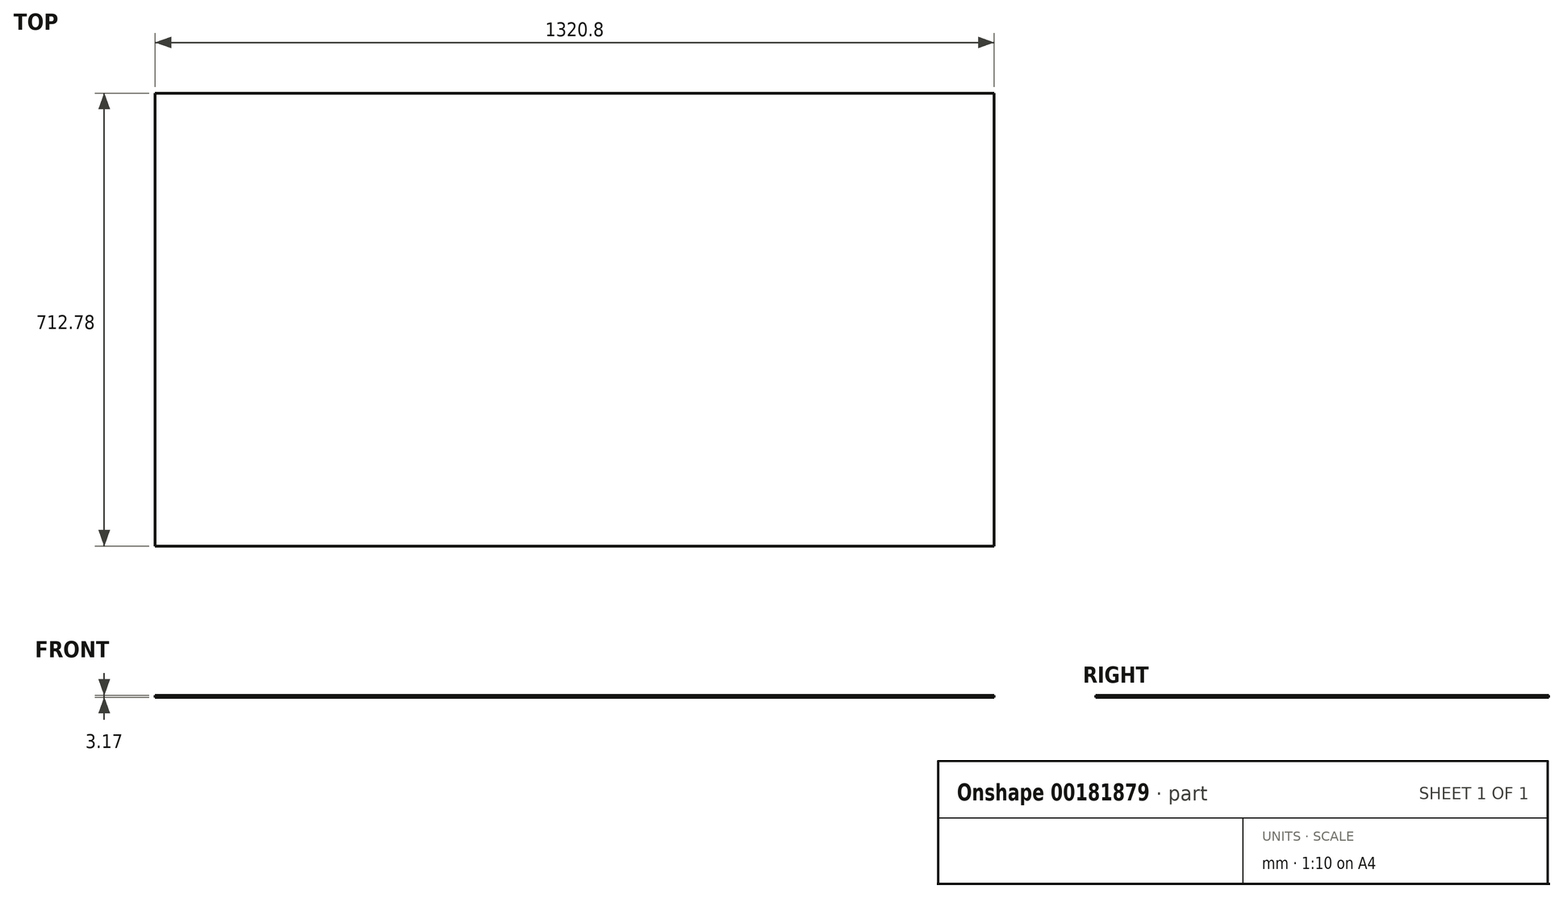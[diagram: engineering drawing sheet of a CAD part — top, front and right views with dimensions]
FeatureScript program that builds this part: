
annotation { "Feature Type Name" : "Feature", "Feature Type Description" : "" }
export const myFeature = defineFeature(function(context is Context, id is Id, definition is map)
    precondition{}
    {
        {
            var Q0;
            Q0=qCreatedBy(makeId("Top.planeOp"),FACE);
            var sketch = newSketch(context, id + "F0", { "sketchPlane" : qUnion([Q0])});
            skLineSegment(sketch, "E0.bottom", {"start": v(660.4, -356.4) * mm, "end": v(-660.4, -356.4) * mm});
            skLineSegment(sketch, "E0.top", {"start": v(660.4, 356.4) * mm, "end": v(-660.4, 356.4) * mm});
            skLineSegment(sketch, "E0.left", {"start": v(660.4, -356.4) * mm, "end": v(660.4, 356.4) * mm});
            skLineSegment(sketch, "E0.right", {"start": v(-660.4, -356.4) * mm, "end": v(-660.4, 356.4) * mm});
            skPoint(sketch, "E0.middle", {"position": v(0, 0) * mm});
            skSolve(sketch);
        }
        {
            var Q0;
            Q0=makeQuery(id+"F0.imprint","IMPRINT",FACE,{"disambiguationData":[TD([[makeQuery(id+"F0.imprint","IMPRINT",EDGE,{"derivedFrom":sQuery(id+"F0.wireOp",EDGE,"E0.bottom")}),-1.0]])]});
            extrude(context, id + "F1", {"entities" : qUnion([Q0]), "oppositeDirection" : true, "depth" : 3.17 * mm});
        }
    });
